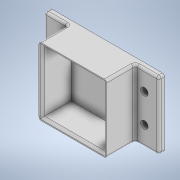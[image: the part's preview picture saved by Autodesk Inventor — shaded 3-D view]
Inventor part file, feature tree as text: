
AUTODESK INVENTOR PART (.ipt)
format: ipt  version: 2020 (Build 240168000, 168)  size: 193,536 bytes
history: native  units: in
note: dims shown in document units (in); Inventor stores cm internally (conversion verified against a paired STEP export)
features: extrude x3, chamfer x3, fillet x3, sketch x3
ambient origin geometry x8: Origin, YZ Plane, XZ Plane, XY Plane, X Axis, Y Axis, Z Axis, Center Point
bodies: Solid1 (feature_tree)
feature tree (12):
  extrude  "Extrusion1"  Depth=2.3228in
  extrude  "Extrusion2"  Depth=2.3228in
  chamfer  "Chamfer1"  Distance=0.1181in
  chamfer  "Chamfer2"  Distance=0.1181in
  chamfer  "Chamfer3"  Distance=0.1181in
  extrude  "Extrusion3"  Depth=0.8071in
  fillet  "Fillet1"  Radius=0.9843in
  fillet  "Fillet2"  Radius=0.0787in
  fillet  "Fillet3"  Radius=0.0787in
  sketch  "Sketch1"  dims[d0=3.937in d1=2.3228in]
  sketch  "Sketch2"  dims[d2=0.1969in d3=0.0in d4=2.3228in]
  sketch  "Sketch3"  dims[d5=2.0866in d6=0.1181in d7=0.1181in d8=0.1181in d9=0.8071in d10=0.9843in d11=0.0in d12=0.0787in d13=0.0787in d14=45.0deg d15=0.0787in d16=0.0787in d17=45.0deg d18=0.0787in d19=0.0787in d20=45.0deg d21=0.2559in d22=0.2559in d23=0.4921in d24=0.4921in d25=0.9843in d26=0.6693in d27=1.9685in d28=2.3622in d29=0.0in d30=0.0787in d31=0.0787in d32=0.0787in]
